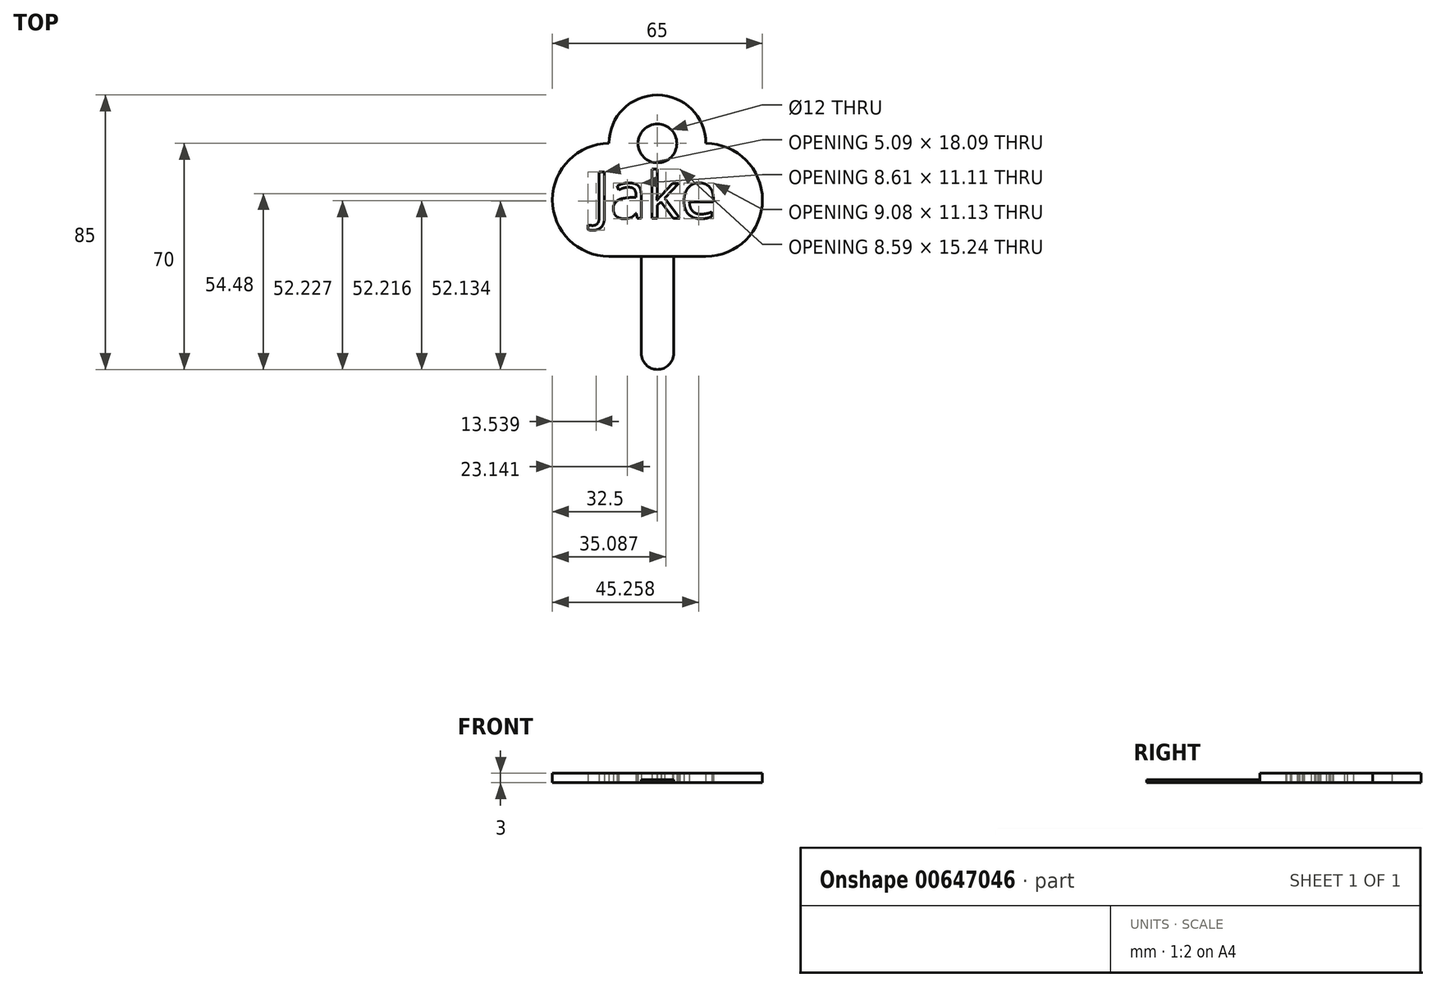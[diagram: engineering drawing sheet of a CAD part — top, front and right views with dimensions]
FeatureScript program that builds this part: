
annotation { "Feature Type Name" : "Feature", "Feature Type Description" : "" }
export const myFeature = defineFeature(function(context is Context, id is Id, definition is map)
    precondition{}
    {
        {
            var Q0;
            Q0=qCreatedBy(makeId("Top.planeOp"),FACE);
            var sketch = newSketch(context, id + "F0", { "sketchPlane" : qUnion([Q0])});
            skLineSegment(sketch, "E0.bottom", {"start": v(15, -17.5) * mm, "end": v(-15, -17.5) * mm});
            skPoint(sketch, "E0.middle", {"position": v(0, 0) * mm});
            skArc(sketch, "E1", {"start": v(15, 17.5) * mm, "mid": v(0, 32.5) * mm, "end": v(-15, 17.5) * mm});
            skArc(sketch, "E2", {"start": v(-15, 17.5) * mm, "mid": v(-32.5, 0) * mm, "end": v(-15, -17.5) * mm});
            skArc(sketch, "E3", {"start": v(15, -17.5) * mm, "mid": v(32.5, 0) * mm, "end": v(15, 17.5) * mm});
            skLineSegment(sketch, "E4.bottom", {"start": v(-15, -17.5) * mm, "end": v(15, -17.5) * mm});
            skLineSegment(sketch, "E4.left", {"start": v(-15, -17.5) * mm, "end": v(-15, -47.5) * mm});
            skLineSegment(sketch, "E4.right", {"start": v(15, -17.5) * mm, "end": v(15, -47.5) * mm});
            skArc(sketch, "E5", {"start": v(-15, -47.5) * mm, "mid": v(0, -62.5) * mm, "end": v(15, -47.5) * mm});
            skLineSegment(sketch, "E6", {"start": v(-15, -17.5) * mm, "end": v(-10, -17.5) * mm});
            skLineSegment(sketch, "E7", {"start": v(-10, -17.5) * mm, "end": v(10, -17.5) * mm});
            skLineSegment(sketch, "E8.left", {"start": v(-10, -17.5) * mm, "end": v(-10, -47.5) * mm});
            skLineSegment(sketch, "E8.right", {"start": v(10, -17.5) * mm, "end": v(10, -47.5) * mm});
            skArc(sketch, "E9", {"start": v(-10, -47.5) * mm, "mid": v(0, -57.5) * mm, "end": v(10, -47.5) * mm});
            skLineSegment(sketch, "E10", {"start": v(-5, -47.5) * mm, "end": v(-5, -17.5) * mm});
            skLineSegment(sketch, "E11", {"start": v(5, -47.5) * mm, "end": v(5, -17.5) * mm});
            skArc(sketch, "E12", {"start": v(-5, -47.5) * mm, "mid": v(0, -52.5) * mm, "end": v(5, -47.5) * mm});
            skCircle(sketch, "E13", {"center": v(0, 17.5) * mm, "radius": 6 * mm});
            skText(sketch, "E14", { "text": "Jake\n", "fontName": "OpenSans-Regular.ttf"});
            const initialGuessF0  = {"E14": [-0.01994, -0.00564, 1, 0, 0.01444]};
            skSetInitialGuess(sketch, initialGuessF0);
            skSolve(sketch);
        }
        {
            var Q0;
            Q0=makeQuery(id+"F0.imprint","IMPRINT",FACE,{"disambiguationData":[TD([[makeQuery(id+"F0.imprint","IMPRINT",EDGE,{"derivedFrom":sQuery(id+"F0.wireOp",EDGE,"E1")}),1.0]])]});
            extrude(context, id + "F1", {"entities" : qUnion([Q0]), "depth" : 3 * mm, "offsetDistance" : 25 * mm});
        }
        {
            var Q0;
            Q0=makeQuery(id+"F0.imprint","IMPRINT",FACE,{"disambiguationData":[TD([[makeQuery(id+"F0.imprint","IMPRINT",EDGE,{"derivedFrom":sQuery(id+"F0.wireOp",EDGE,"E4.bottom")}),-1.0]])]});
            var Q1;
            {var subQ0=sQuery(id+"F0.wireOp",EDGE,"E10");Q1=makeQuery(id+"F0.imprint","IMPRINT",FACE,{"disambiguationData":[TD([[makeQuery(id+"F0.imprint","IMPRINT",EDGE,{"derivedFrom":subQ0}),-1.0]])]});}
            extrude(context, id + "F2", {"entities" : qUnion([Q0, Q1]), "operationType" : NewBodyOperationType.ADD, "depth" : 1 * mm, "offsetDistance" : 25 * mm});
        }
    });
